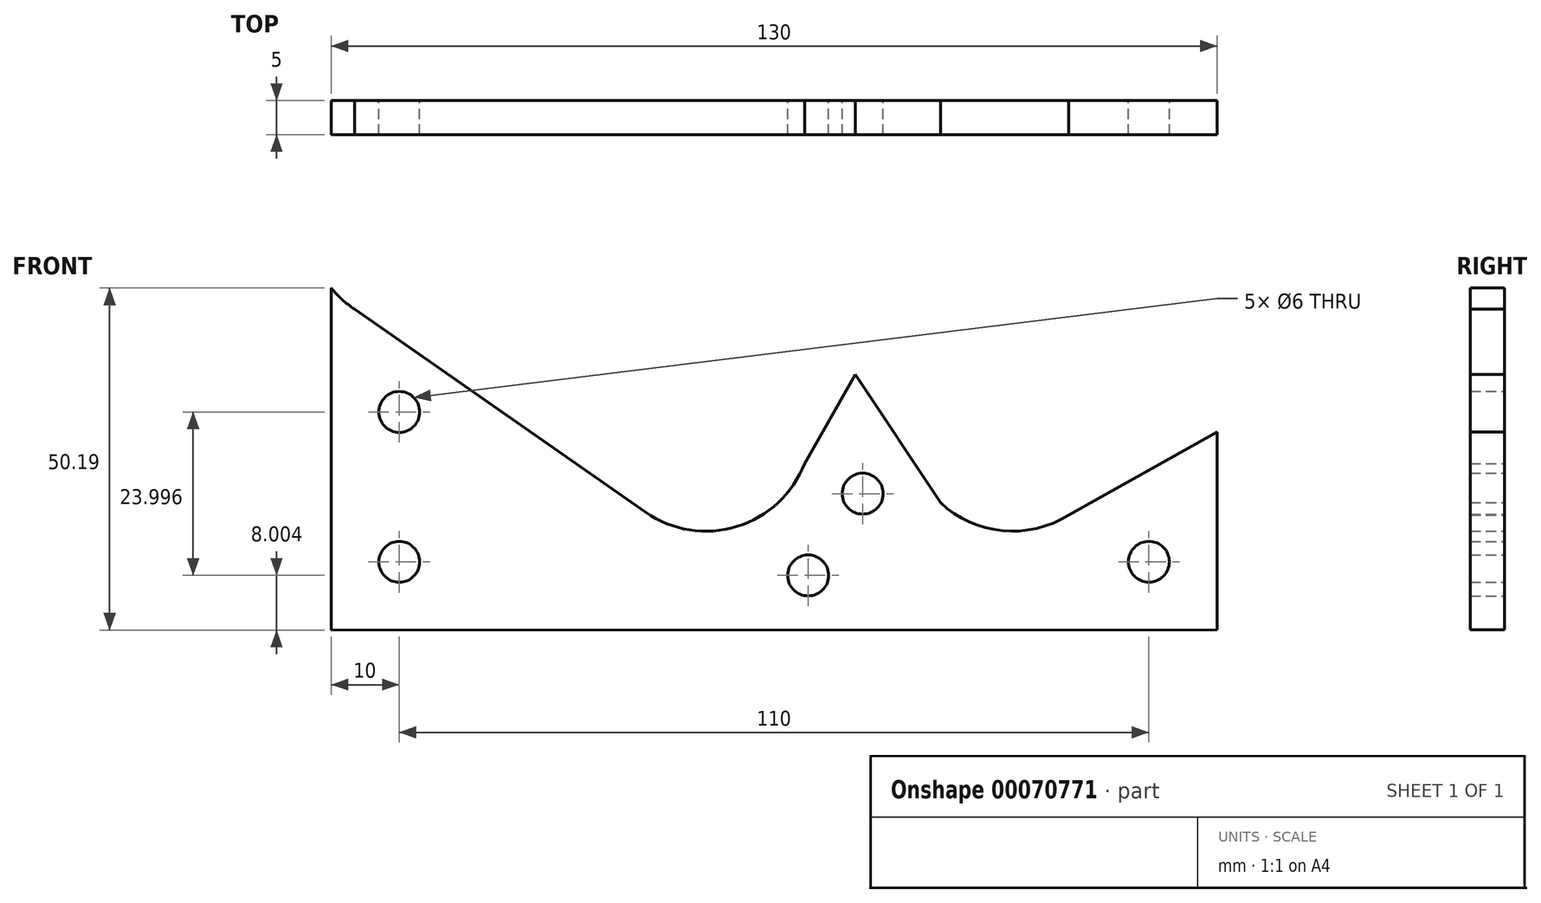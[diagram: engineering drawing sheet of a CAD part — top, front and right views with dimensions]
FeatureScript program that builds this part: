
annotation { "Feature Type Name" : "Feature", "Feature Type Description" : "" }
export const myFeature = defineFeature(function(context is Context, id is Id, definition is map)
    precondition{}
    {
        {
            var Q0;
            Q0=qCreatedBy(makeId("Front.planeOp"),FACE);
            var sketch = newSketch(context, id + "F0", { "sketchPlane" : qUnion([Q0])});
            skLineSegment(sketch, "E0.bottom", {"start": v(0, 0) * mm, "end": v(130, 0) * mm});
            skLineSegment(sketch, "E0.left", {"start": v(0, 0) * mm, "end": v(0, 50.19) * mm});
            skLineSegment(sketch, "E0.right", {"start": v(130, 0) * mm, "end": v(130, 29.08) * mm});
            skArc(sketch, "E1", {"start": v(46.13, 17.29) * mm, "mid": v(59.54, 15.18) * mm, "end": v(69.47, 24.44) * mm});
            skLineSegment(sketch, "E2", {"start": v(106.9, 16.13) * mm, "end": v(130, 29.08) * mm});
            skLineSegment(sketch, "E3", {"start": v(89.42, 18.68) * mm, "end": v(76.95, 37.47) * mm});
            skArc(sketch, "E4", {"start": v(89.42, 18.68) * mm, "mid": v(98.52, 14.58) * mm, "end": v(108.24, 16.88) * mm});
            skArc(sketch, "E5", {"start": v(0, 50.19) * mm, "mid": v(1.6, 48.5) * mm, "end": v(3.45, 47.07) * mm});
            skLineSegment(sketch, "E6", {"start": v(3.45, 47.07) * mm, "end": v(46.13, 17.29) * mm});
            skLineSegment(sketch, "E7", {"start": v(67.1, 20.32) * mm, "end": v(76.95, 37.47) * mm});
            skCircle(sketch, "E8", {"center": v(10, 10) * mm, "radius": 3 * mm});
            skCircle(sketch, "E9", {"center": v(78, 20) * mm, "radius": 3 * mm});
            skCircle(sketch, "E10", {"center": v(120, 10) * mm, "radius": 3 * mm});
            skCircle(sketch, "E11", {"center": v(10, 32) * mm, "radius": 3 * mm});
            skCircle(sketch, "E12", {"center": v(70, 8) * mm, "radius": 3 * mm});
            skSolve(sketch);
        }
        {
            var Q0;
            {var subQ1=sQuery(id+"F0.wireOp",EDGE,"E0.bottom");Q0=makeQuery(id+"F0.imprint","IMPRINT",FACE,{"disambiguationData":[TD([[makeQuery(id+"F0.imprint","IMPRINT",EDGE,{"derivedFrom":subQ1}),1.0]])]});}
            extrude(context, id + "F1", {"entities" : qUnion([Q0]), "depth" : 5 * mm});
        }
    });
